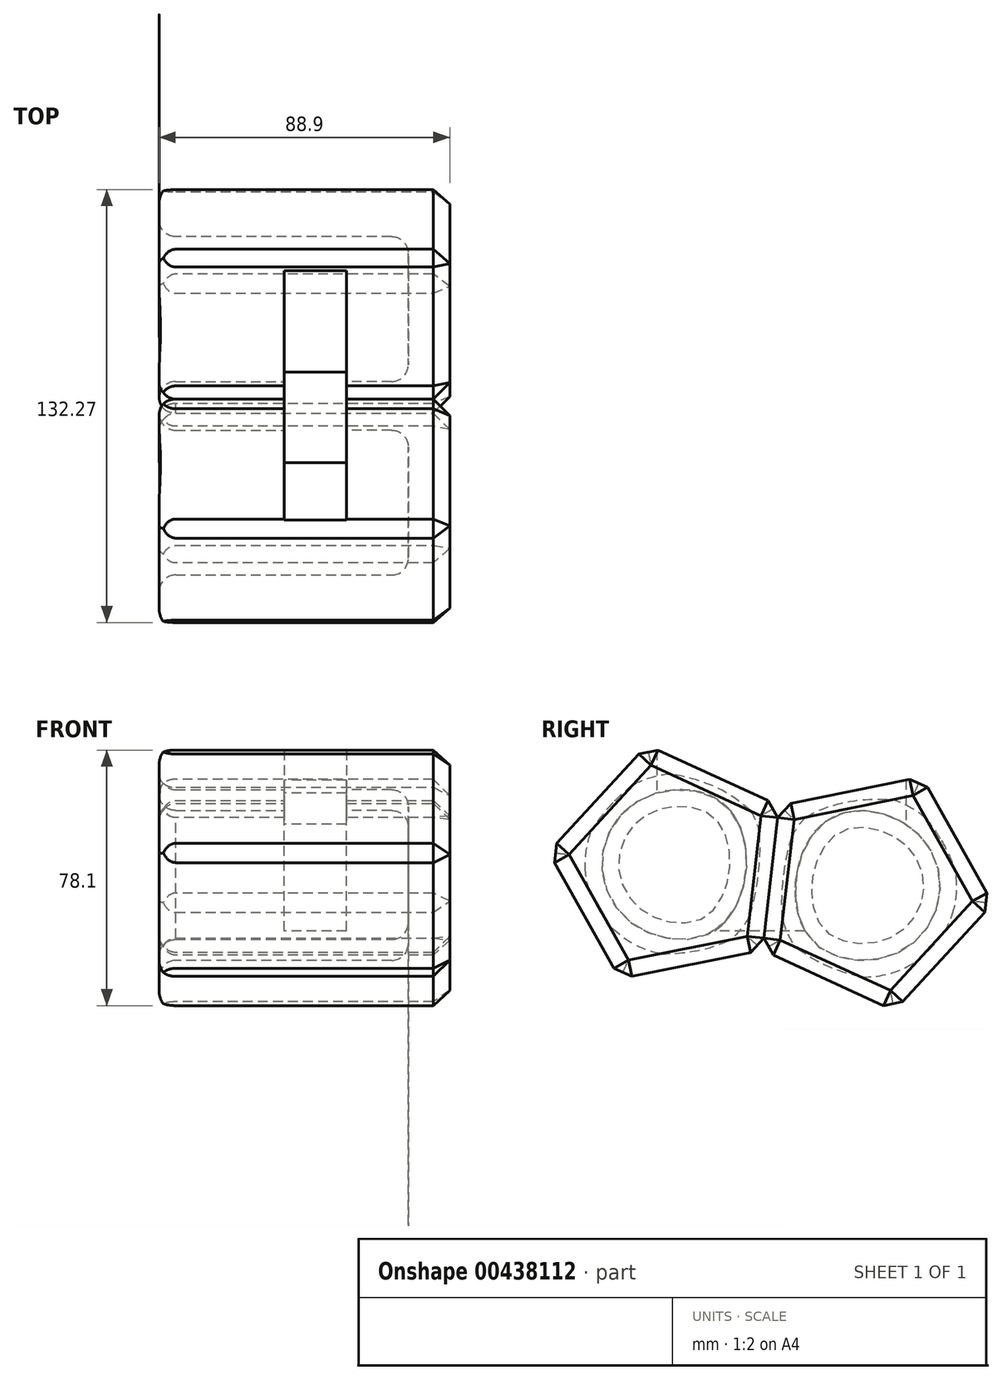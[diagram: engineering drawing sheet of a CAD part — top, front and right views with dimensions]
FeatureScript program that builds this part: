
annotation { "Feature Type Name" : "Feature", "Feature Type Description" : "" }
export const myFeature = defineFeature(function(context is Context, id is Id, definition is map)
    precondition{}
    {
        {
            var Q0;
            Q0=qCreatedBy(makeId("Right.planeOp"),FACE);
            var sketch = newSketch(context, id + "F0", { "sketchPlane" : qUnion([Q0])});
            skCircle(sketch, "E0.cCircle", {"center": v(0, 0) * mm, "radius": 30.6 * mm, "construction": true});
            skLineSegment(sketch, "E0.0", {"start": v(15.74, 34.38) * mm, "end": v(37.56, -4.35) * mm});
            skLineSegment(sketch, "E0.1", {"start": v(37.56, -4.35) * mm, "end": v(7.47, -37.07) * mm});
            skLineSegment(sketch, "E0.2", {"start": v(7.47, -37.07) * mm, "end": v(-32.94, -18.56) * mm});
            skLineSegment(sketch, "E0.3", {"start": v(-32.94, -18.56) * mm, "end": v(-27.83, 25.6) * mm});
            skLineSegment(sketch, "E0.4", {"start": v(-27.83, 25.6) * mm, "end": v(15.74, 34.38) * mm});
            skPoint(sketch, "E0.0.midPoint", {"position": v(26.65, 15.01) * mm});
            skSolve(sketch);
        }
        {
            var Q0;
            Q0=makeQuery(id+"F0.imprint","IMPRINT",FACE,{"disambiguationData":[TD([[makeQuery(id+"F0.imprint","IMPRINT",EDGE,{"derivedFrom":sQuery(id+"F0.wireOp",EDGE,"E0.0")}),-1.0]])]});
            extrude(context, id + "F1", {"entities" : qUnion([Q0]), "depth" : 88.9 * mm});
        }
        {
            var Q0;
            Q0=makeQuery(id+"F1.opExtrude","CAP_FACE",FACE,{"disambiguationData":[OSD([sQuery(id+"F0.wireOp",EDGE,"E0.0"),sQuery(id+"F0.wireOp",EDGE,"E0.1"),sQuery(id+"F0.wireOp",EDGE,"E0.2"),sQuery(id+"F0.wireOp",EDGE,"E0.3"),sQuery(id+"F0.wireOp",EDGE,"E0.4")])],"isStart":true});
            var sketch = newSketch(context, id + "F2", { "sketchPlane" : qUnion([Q0])});
            skFitSpline(sketch, "E1", {"points": [v(-20.29, -6.13) * mm, v(-5.66, -20.51) * mm, v(17.3, -16.21) * mm, v(22, 7.04) * mm, v(10.6, 22.55) * mm, v(-6.3, 22.29) * mm, v(-18.82, 11.47) * mm, v(-20.29, -6.13) * mm]});
            skSolve(sketch);
        }
        {
            var Q0;
            Q0=makeQuery(id+"F2.imprint","IMPRINT",FACE,{"disambiguationData":[TD([[makeQuery(id+"F2.imprint","IMPRINT",EDGE,{"derivedFrom":sQuery(id+"F2.wireOp",EDGE,"E1")}),1.0]])]});
            extrude(context, id + "F3", {"entities" : qUnion([Q0]), "operationType" : NewBodyOperationType.REMOVE, "oppositeDirection" : true, "depth" : 76.2 * mm});
        }
        {
            var Q0;
            Q0=makeQuery(id+"F1.opExtrude","CAP_FACE",FACE,{"disambiguationData":[OSD([sQuery(id+"F0.wireOp",EDGE,"E0.0"),sQuery(id+"F0.wireOp",EDGE,"E0.1"),sQuery(id+"F0.wireOp",EDGE,"E0.2"),sQuery(id+"F0.wireOp",EDGE,"E0.3"),sQuery(id+"F0.wireOp",EDGE,"E0.4")])],"isStart":true});
            var Q1;
            Q1=makeQuery(id+"F3.boolean.opBoolean","COPY",FACE,{"derivedFrom":makeQuery(id+"F3.opExtrude","CAP_FACE",FACE,{"disambiguationData":[OSD([sQuery(id+"F2.wireOp",EDGE,"E1")])],"isStart":false})});
            fillet(context, id + "F4", {"entities" : qUnion([Q0, Q1]), "radius" : 5.08 * mm, "tangentPropagation" : true, "allowEdgeOverflow" : false});
        }
        {
            var Q0;
            Q0=makeQuery(id+"F1.opExtrude","SWEPT_FACE",FACE,{"disambiguationData":[OSD([sQuery(id+"F0.wireOp",EDGE,"E0.0")])]});
            var Q1;
            Q1=makeQuery(id+"F1.opExtrude","SWEPT_FACE",FACE,{"disambiguationData":[OSD([sQuery(id+"F0.wireOp",EDGE,"E0.4")])]});
            var Q2;
            Q2=makeQuery(id+"F1.opExtrude","SWEPT_FACE",FACE,{"disambiguationData":[OSD([sQuery(id+"F0.wireOp",EDGE,"E0.2")])]});
            var Q3;
            Q3=makeQuery(id+"F1.opExtrude","SWEPT_FACE",FACE,{"disambiguationData":[OSD([sQuery(id+"F0.wireOp",EDGE,"E0.1")])]});
            var Q4;
            Q4=makeQuery(id+"F1.opExtrude","SWEPT_FACE",FACE,{"disambiguationData":[OSD([sQuery(id+"F0.wireOp",EDGE,"E0.3")])]});
            chamfer(context, id + "F5", {"entities" : qUnion([Q0, Q1, Q2, Q3, Q4]), "width" : 5.08 * mm, "tangentPropagation" : true});
        }
        {
            var Q0;
            Q0=makeQuery(id+"F1.opExtrude","SWEPT_BODY",BODY,{"disambiguationData":[OSD([sQuery(id+"F0.wireOp",EDGE,"E0.0"),sQuery(id+"F0.wireOp",EDGE,"E0.1"),sQuery(id+"F0.wireOp",EDGE,"E0.2"),sQuery(id+"F0.wireOp",EDGE,"E0.3"),sQuery(id+"F0.wireOp",EDGE,"E0.4")])]});
            var Q1;
            Q1=makeQuery(id+"F1.opExtrude","SWEPT_FACE",FACE,{"disambiguationData":[OSD([sQuery(id+"F0.wireOp",EDGE,"E0.3")])]});
            mirror(context, id + "F6", {"operationType" : NewBodyOperationType.ADD, "entities" : qUnion([Q0]), "mirrorPlane" : qUnion([Q1])});
        }
        {
            var Q0;
            Q0=qCreatedBy(makeId("Top.planeOp"),FACE);
            var sketch = newSketch(context, id + "F7", { "sketchPlane" : qUnion([Q0])});
            skLineSegment(sketch, "E2.bottom", {"start": v(38.24, 11) * mm, "end": v(57.3, 11) * mm});
            skLineSegment(sketch, "E2.top", {"start": v(38.24, -65.2) * mm, "end": v(57.3, -65.2) * mm});
            skLineSegment(sketch, "E2.left", {"start": v(38.24, 11) * mm, "end": v(38.24, -65.2) * mm});
            skLineSegment(sketch, "E2.right", {"start": v(57.3, 11) * mm, "end": v(57.3, -65.2) * mm});
            skSolve(sketch);
        }
        {
            var Q0;
            Q0=makeQuery(id+"F7.imprint","IMPRINT",FACE,{"disambiguationData":[TD([[makeQuery(id+"F7.imprint","IMPRINT",EDGE,{"derivedFrom":sQuery(id+"F7.wireOp",EDGE,"E2.bottom")}),-1.0]])]});
            var Q1;
            Q1=sQuery(id+"F7.wireOp",EDGE,"E2.right");
            var Q2;
            Q2=sQuery(id+"F7.wireOp",EDGE,"E2.top");
            var Q3;
            Q3=sQuery(id+"F7.wireOp",EDGE,"E2.left");
            var Q4;
            Q4=sQuery(id+"F7.wireOp",EDGE,"E2.bottom");
            extrude(context, id + "F8", {"entities" : qUnion([Q0]), "operationType" : NewBodyOperationType.REMOVE, "surfaceEntities" : qUnion([Q1, Q2, Q3, Q4]), "depth" : 101.6 * mm});
        }
        {
            var Q0;
            Q0 = qSketchRegion(id + "F7", true);
            extrude(context, id + "F9", {"entities" : qUnion([Q0]), "operationType" : NewBodyOperationType.REMOVE, "oppositeDirection" : true, "depth" : 12.7 * mm});
        }
    });
